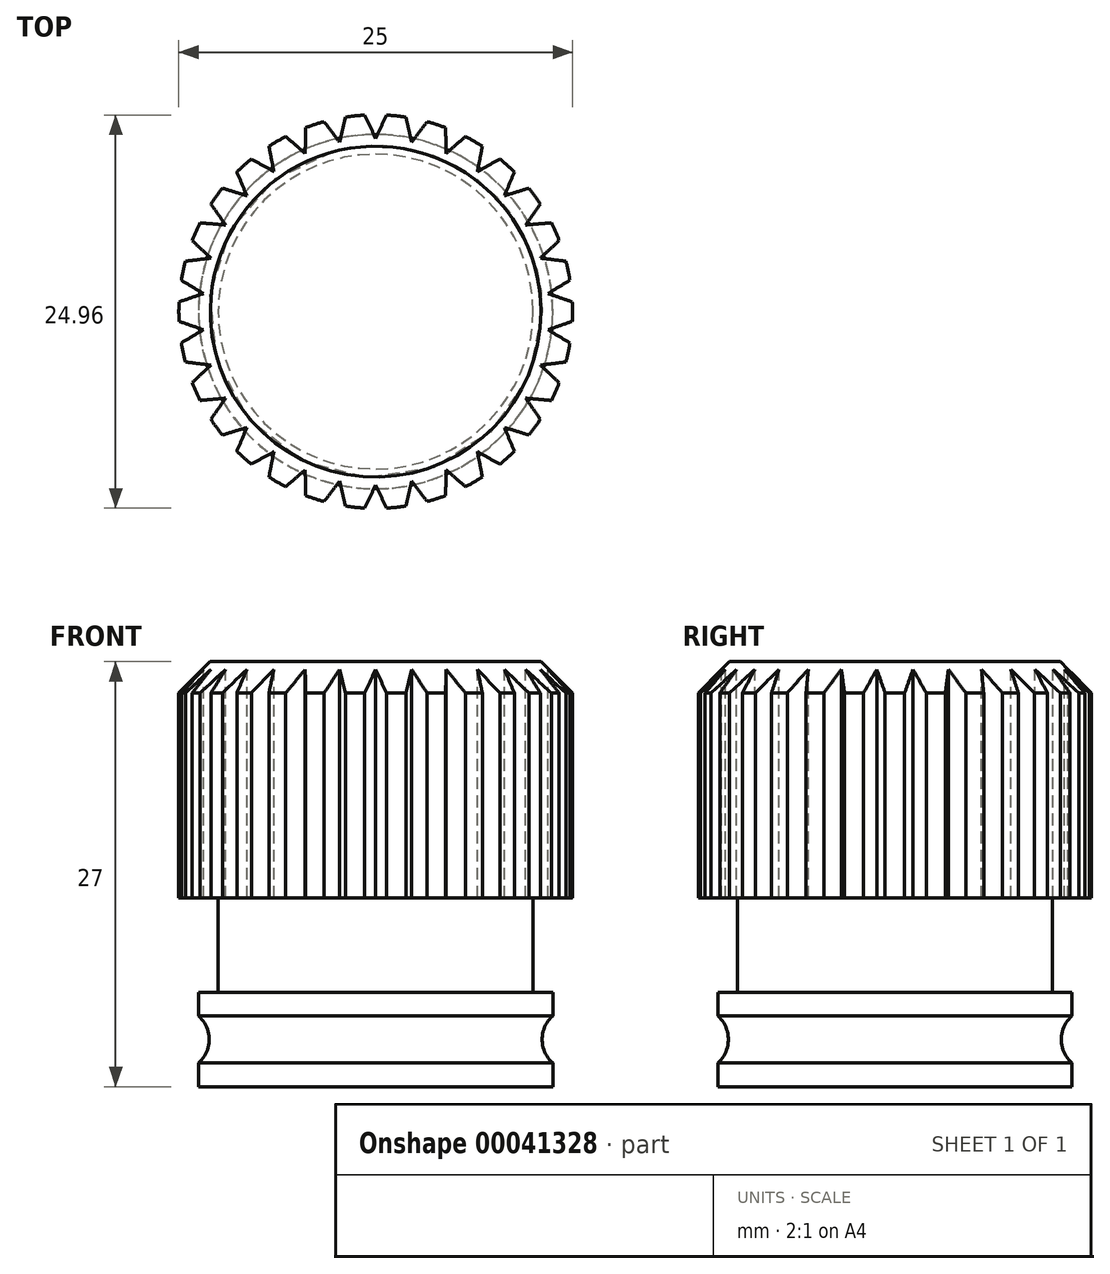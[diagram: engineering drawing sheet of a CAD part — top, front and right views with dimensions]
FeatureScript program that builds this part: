
annotation { "Feature Type Name" : "Feature", "Feature Type Description" : "" }
export const myFeature = defineFeature(function(context is Context, id is Id, definition is map)
    precondition{}
    {
        {
            assignVariable(context, id + "F0", {"name" : "ButtonHeight", "anyValue" : 15});
        }
        {
            assignVariable(context, id + "F1", {"name" : "ToothNumber", "anyValue" : 60});
        }
        {
            var Q0;
            Q0=qCreatedBy(makeId("Front.planeOp"),FACE);
            var sketch = newSketch(context, id + "F2", { "sketchPlane" : qUnion([Q0])});
            skLineSegment(sketch, "E0", {"start": v(0, 0) * mm, "end": v(-11.25, 0) * mm});
            skLineSegment(sketch, "E1", {"start": v(-11.25, 0) * mm, "end": v(-11.25, 1.5) * mm});
            skArc(sketch, "E2", {"start": v(-11.25, 1.5) * mm, "mid": v(-10.57, 3) * mm, "end": v(-11.25, 4.5) * mm});
            skLineSegment(sketch, "E3", {"start": v(-11.25, 4.5) * mm, "end": v(-11.25, 6) * mm});
            skLineSegment(sketch, "E4", {"start": v(-11.25, 6) * mm, "end": v(-10, 6) * mm});
            skLineSegment(sketch, "E5", {"start": v(-10, 6) * mm, "end": v(-10, 12) * mm});
            skLineSegment(sketch, "E6", {"start": v(-10, 12) * mm, "end": v(-12.5, 12) * mm});
            skLineSegment(sketch, "E7", {"start": v(-12.5, 12) * mm, "end": v(-12.5, 27) * mm});
            skLineSegment(sketch, "E8", {"start": v(-12.5, 27) * mm, "end": v(0, 27) * mm});
            skLineSegment(sketch, "E9", {"start": v(0, 27) * mm, "end": v(0, 0) * mm});
            skLineSegment(sketch, "E10", {"start": v(-12.5, 25) * mm, "end": v(-10.5, 27) * mm});
            skSolve(sketch);
        }
        {
            var Q0;
            Q0=makeQuery(id+"F2.imprint","IMPRINT",FACE,{"disambiguationData":[TD([[makeQuery(id+"F2.imprint","IMPRINT",EDGE,{"derivedFrom":sQuery(id+"F2.wireOp",EDGE,"E0")}),-1.0]])]});
            var Q1;
            Q1=sQuery(id+"F2.wireOp",EDGE,"E9");
            revolve(context, id + "F3", {"entities" : qUnion([Q0]), "axis" : qUnion([Q1]), "revolveType" : RevolveType.FULL});
        }
        {
            var Q0;
            Q0=makeQuery(id+"F3.opRevolve","SWEPT_FACE",FACE,{"disambiguationData":[OSD([sQuery(id+"F2.wireOp",EDGE,"E8")])]});
            var sketch = newSketch(context, id + "F4", { "sketchPlane" : qUnion([Q0])});
            skCircle(sketch, "E11", {"center": v(0, 0) * mm, "radius": 12.5 * mm});
            skLineSegment(sketch, "E12", {"start": v(-0.7, 12.48) * mm, "end": v(0, 11) * mm});
            skLineSegment(sketch, "E13", {"start": v(0, 11) * mm, "end": v(0.7, 12.48) * mm});
            skSolve(sketch);
        }
        {
            var Q0;
            {var subQ1=sQuery(id+"F4.wireOp",EDGE,"E12");Q0=makeQuery(id+"F4.imprint","IMPRINT",FACE,{"disambiguationData":[TD([[makeQuery(id+"F4.imprint","IMPRINT",EDGE,{"derivedFrom":subQ1}),1.0]])]});}
            extrude(context, id + "F5", {"entities" : qUnion([Q0]), "operationType" : NewBodyOperationType.REMOVE, "oppositeDirection" : true, "depth" : (getVariable(context, 'ButtonHeight')) * mm});
        }
        {
            var Q0;
            Q0=makeQuery(id+"F5.boolean.opBoolean","COPY",FACE,{"derivedFrom":makeQuery(id+"F5.opExtrude","SWEPT_FACE",FACE,{"disambiguationData":[OSD([sQuery(id+"F4.wireOp",EDGE,"E13")])]})});
            var Q1;
            Q1=makeQuery(id+"F5.boolean.opBoolean","COPY",FACE,{"derivedFrom":makeQuery(id+"F5.opExtrude","SWEPT_FACE",FACE,{"disambiguationData":[OSD([sQuery(id+"F4.wireOp",EDGE,"E12")])]})});
            var Q2;
            Q2=makeQuery(id+"F3.opRevolve","SWEPT_EDGE",EDGE,{"disambiguationData":[OSD([sQuery(id+"F2.wireOp",EDGE,"E8"),sQuery(id+"F2.wireOp",EDGE,"E10")])]});
            circularPattern(context, id + "F6", {"operationType" : NewBodyOperationType.REMOVE, "faces" : qUnion([Q0, Q1]), "axis" : qUnion([Q2]), "angle" : 360 * degree, "instanceCount" : getVariable(context, 'ToothNumber'), "equalSpace" : true, "patternType" : PatternType.FACE});
        }
    });
